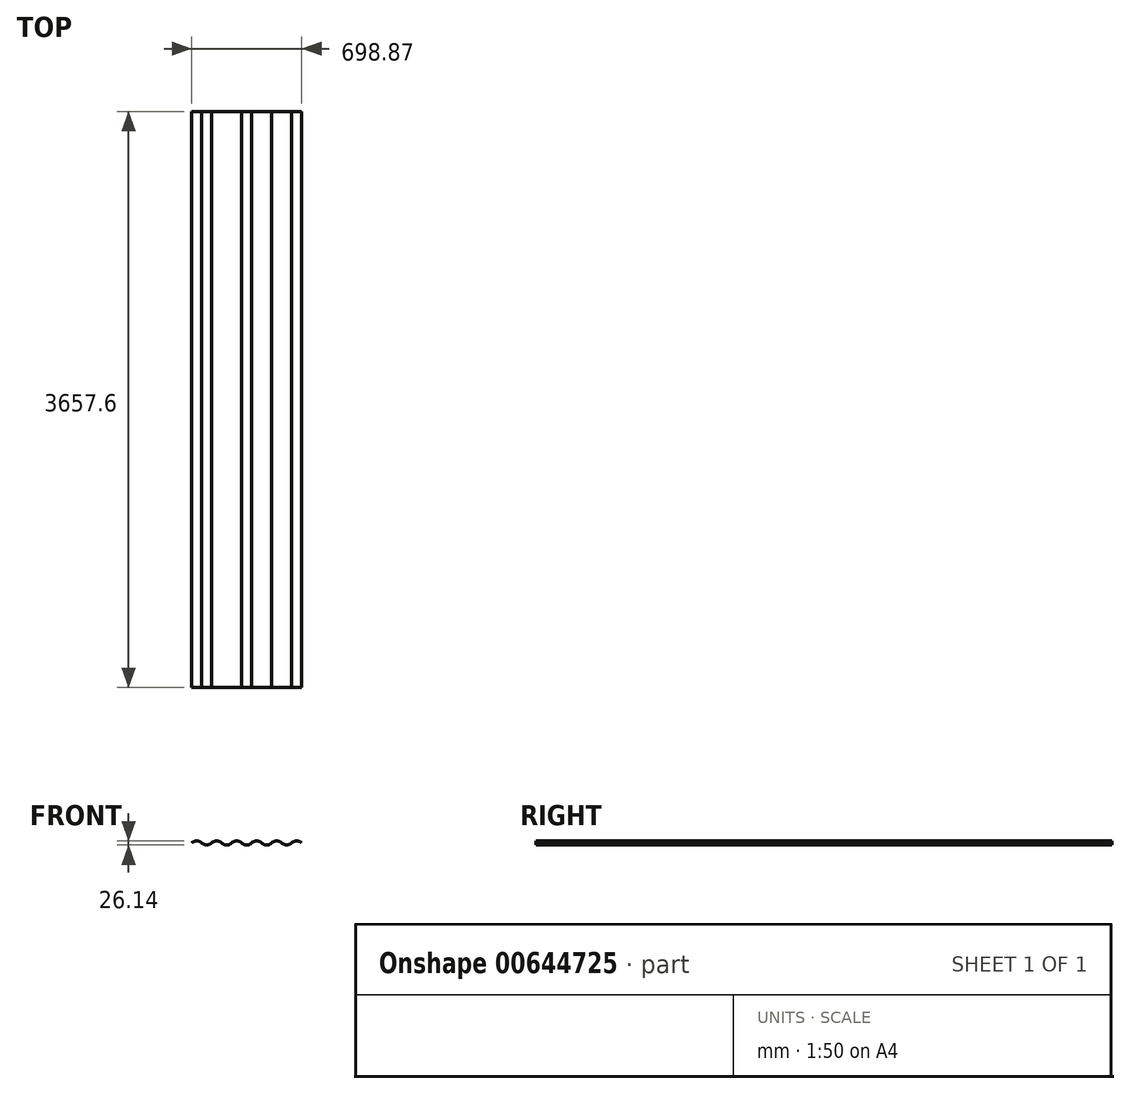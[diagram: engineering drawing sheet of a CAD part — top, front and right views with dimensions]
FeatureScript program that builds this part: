
annotation { "Feature Type Name" : "Feature", "Feature Type Description" : "" }
export const myFeature = defineFeature(function(context is Context, id is Id, definition is map)
    precondition{}
    {
        {
            var Q0;
            Q0=qCreatedBy(makeId("Front.planeOp"),FACE);
            var sketch = newSketch(context, id + "F0", { "sketchPlane" : qUnion([Q0])});
            skPoint(sketch, "E0", {"position": v(0, 12.65) * mm});
            skPoint(sketch, "E1", {"position": v(-31.76, 0) * mm});
            skPoint(sketch, "E2", {"position": v(31.76, 0) * mm});
            skArc(sketch, "E3", {"start": v(-31.76, -0.28) * mm, "mid": v(0, -12.93) * mm, "end": v(31.76, -0.28) * mm});
            skArc(sketch, "E4", {"start": v(95.3, 0) * mm, "mid": v(63.54, 12.65) * mm, "end": v(31.78, 0) * mm});
            skArc(sketch, "E5", {"start": v(-31.8, 0) * mm, "mid": v(-63.55, 12.65) * mm, "end": v(-95.31, 0) * mm});
            skArc(sketch, "E6", {"start": v(95.3, 0) * mm, "mid": v(127.06, -12.65) * mm, "end": v(158.82, 0) * mm});
            skArc(sketch, "E7", {"start": v(222.36, 0.28) * mm, "mid": v(190.6, 12.93) * mm, "end": v(158.84, 0.28) * mm});
            skArc(sketch, "E8", {"start": v(-158.83, 0) * mm, "mid": v(-127.07, -12.65) * mm, "end": v(-95.31, 0) * mm});
            skArc(sketch, "E9", {"start": v(222.36, 0.28) * mm, "mid": v(254.12, -12.37) * mm, "end": v(285.88, 0.28) * mm});
            skArc(sketch, "E10", {"start": v(349.41, 0.56) * mm, "mid": v(317.65, 13.2) * mm, "end": v(285.9, 0.56) * mm});
            skArc(sketch, "E11", {"start": v(-285.9, 0.28) * mm, "mid": v(-254.15, -12.37) * mm, "end": v(-222.39, 0.28) * mm});
            skArc(sketch, "E12", {"start": v(-285.94, 0.56) * mm, "mid": v(-317.7, 13.2) * mm, "end": v(-349.46, 0.56) * mm});
            skPoint(sketch, "E13.endSnap0", {"position": v(-187.9, 12.85) * mm});
            skArc(sketch, "E14", {"start": v(-158.83, 0) * mm, "mid": v(-190.6, 12.65) * mm, "end": v(-222.35, 0) * mm});
            skSolve(sketch);
        }
        {
            var Q0;
            Q0=sQuery(id+"F0.wireOp",EDGE,"E8");
            var Q1;
            Q1=sQuery(id+"F0.wireOp",EDGE,"E7");
            var Q2;
            Q2=sQuery(id+"F0.wireOp",EDGE,"E3");
            var Q3;
            Q3=sQuery(id+"F0.wireOp",EDGE,"E9");
            var Q4;
            Q4=sQuery(id+"F0.wireOp",EDGE,"E5");
            var Q5;
            Q5=sQuery(id+"F0.wireOp",EDGE,"E6");
            var Q6;
            Q6=sQuery(id+"F0.wireOp",EDGE,"E10");
            var Q7;
            Q7=sQuery(id+"F0.wireOp",EDGE,"E11");
            var Q8;
            Q8=sQuery(id+"F0.wireOp",EDGE,"E12");
            var Q9;
            Q9=sQuery(id+"F0.wireOp",EDGE,"E4");
            var Q10;
            Q10=sQuery(id+"F0.wireOp",EDGE,"E14");
            extrude(context, id + "F1", {"bodyType" : ToolBodyType.SURFACE, "surfaceEntities" : qUnion([Q0, Q1, Q2, Q3, Q4, Q5, Q6, Q7, Q8, Q9, Q10]), "depth" : 0 * mm, "offsetDistance" : 25.4 * mm, "hasSecondDirection" : true, "secondDirectionOppositeDirection" : true, "secondDirectionDepth" : 3657.6 * mm});
        }
    });
